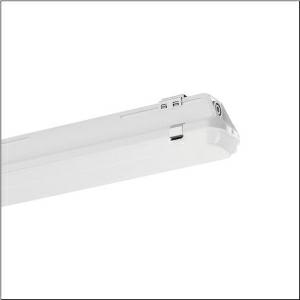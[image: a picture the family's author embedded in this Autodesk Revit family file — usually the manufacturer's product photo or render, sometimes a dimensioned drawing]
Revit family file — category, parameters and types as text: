
# Revit family: monsun_r__11_emergency_51fp107p467l3g_737b
name_source: partatom
category: Lighting Fixtures
units: mm (PartAtom-declared; Revit-internal decimal feet)

## family parameters
Cut with Voids When Loaded = No
Host = Face
Light Source = No
Part Type = Normal
Room Calculation Point = No
Round Connector Dimension = Use Diameter
Shared = No

## types (1)
- --- (1 x LED, 990 lm, 6.5 W, 4000K)
    Apparent Load = 7 VA
    CIE Flux Codes = 47 77 93 94 100
    Color Rendering = 80
    Color Temperature = 4000K
    Default Elevation = 1800 mm
    Description = Monsun® 11 emergency, damp-proof luminaire, chain hanger, primary optical cover: enclosure, of PMMA, light emission: direct distribution, primary light characteristic: symmetric, installation type: suspended mounting, surface-mounted, horizontal mounting, vertical mounting, LED, rated luminous flux: 6.050lm, luminous efficacy: 179lm/W, light colour: 840, colour temperature: 4000K, control gear: ON/OFF, with terminal, 4-pole, max. 2.5mm², mains connection: 220..240V, AC, 50/60Hz, rated input power: 37W, control gear: single battery element, battery: LiFePO4, 9Ah, luminaire housing, of glass-fibre reinforced polyester, uncoated, bright grey, incl. chain hanger, length: 1.590mm, width: 90mm, height: 88mm, clip for enclosure, of stainless steel (V2A), ceiling mounting element, of stainless steel (V2A), chain hanger, of stainless steel (V2A), protection rating (complete): IP66, insulation class (complete): insulation class I (protective earthing), certification: CE, UKCA, protection symbol: D, impact resistance: IK04, permissible operating ambient temperature: +5..+35°C, standard: EN 50419, EN 60598-2-1, EN 60598-2-22, contact your sales advisor before using the luminaires in applications with unclear chemical exposure, large temperature fluctuations or condensation-forming humidity, LABS conformity tested according to VDMA 24364:2018-05, no direct snow, no direct sun, no direct rain, for indoor or canopied outdoor use, corresponds to IFS (International Featured Standards) requirements for safety and quality in the food industry, packaging unit: 1 piece
    Height = 89 mm
    Lamp = 1 x LED
    Lamp Light Flux = 990 lm
    Lamp Power = 6.5 W
    Lamp count = 1
    Length = 1590 mm
    Luminous efficacy = 152 lm/W
    Manufacturer = Siteco
    ModVariant = No
    Model = 51FP107P467L3G
    Mounting Place = Ceiling
    Mounting Type = Surface mounted
    Number of Poles = 1
    OnlyDefault = Yes
    Power Factor = 1
    Product Name = Monsun® 11 emergency
    Product group = damp-proof luminaire
    ProductGroupID = 301
    Protection Class = Protection class I
    Protection Degree = IP 66
    RLX_Detail_Level = 1
    RLX_Emergency_Light_Flux = 0 lm
    RLX_Emergency_Type = 0
    RLX_Emergency_Type_DB = No
    RlxData = <blob elided: 88989 chars, md5=4cc4ee17>
    Socket = socket
    Standby Power = 0 W
    System Light Flux = 990 lm
    System Power = 7 W
    Type Comments = : emergency light operation: 3 h
    Type Image = l_1349237.jpg
    URL = http://relux.com
    VarID = @adj_038131
    Voltage = 0 V
    Weight = 0.00 kg
    Width = 90 mm

## geometry (parser evidence)
native form markers: Blend x4, Sweep x12
no freeform markers — native parametric forms only
